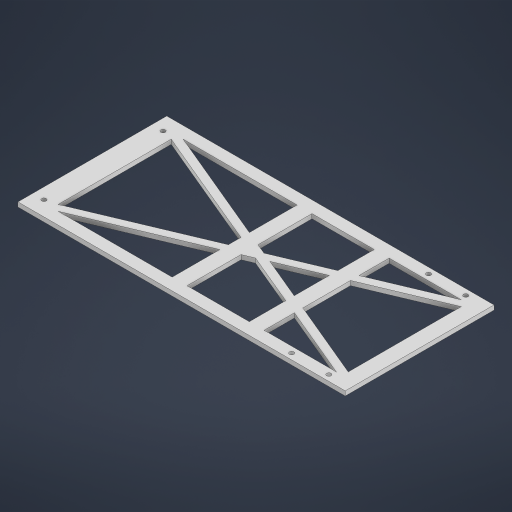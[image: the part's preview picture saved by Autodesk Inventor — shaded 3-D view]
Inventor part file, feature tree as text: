
AUTODESK INVENTOR PART (.ipt)
format: ipt  version: 2023 (Build 270158000, 158)  size: 261,120 bytes
history: native  units: in
note: dims shown in document units (in); Inventor stores cm internally (conversion verified against a paired STEP export)
features: sketch x2, other x1, extrude x1
ambient origin geometry x8: Origin, YZ Plane, XZ Plane, XY Plane, X Axis, Y Axis, Z Axis, Center Point
bodies: Body1 (feature_tree)
feature tree (4):
  other  "Bryła1"
  sketch  "Szkic1"
  extrude  "Wyciągnięcie proste1"  Depth=0.5906in
  sketch  "Szkic2"
